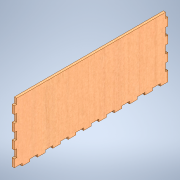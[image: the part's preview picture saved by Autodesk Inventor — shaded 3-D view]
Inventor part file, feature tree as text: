
AUTODESK INVENTOR PART (.ipt)
format: ipt  version: 2021 (Build 250183000, 183)  size: 227,840 bytes
history: native  units: mm
features: extrude x3, sketch x3, other x1
ambient origin geometry x8: Origin, YZ Plane, XZ Plane, XY Plane, X Axis, Y Axis, Z Axis, Center Point
bodies: Solid1 (feature_tree)
feature tree (7):
  other  "DoosjeRechterkant"
  extrude  "Extrusion1"  Depth=200.0mm
  extrude  "Extrusion2"  Depth=10.0mm
  extrude  "Extrusion3"  Depth=10.0mm
  sketch  "Sketch1"  dims[d0=77.0mm d1=200.0mm]
  sketch  "Sketch2"  dims[d2=3.0mm d3=0.0mm d4=10.0mm]
  sketch  "Sketch3"  dims[d7=100.0mm d9=20.0mm d10=10.0mm d12=10.0mm d14=10.0mm d15=3.0mm d16=10.0mm d17=30.0mm d19=20.0mm d20=10.0mm d22=10.0mm d24=10.0mm d25=10.0mm d26=3.0mm d27=0.0mm d28=10.0mm d29=3.0mm d30=10.0mm d31=20.0mm d32=3.0mm d33=0.0mm]
